# Revit family: PRD_AR_PprTwlDspnsrs_RODANElectronicPaperTowelDispenser_RODX630
name_source: partatom
category: Specialty Equipment
revit_build: Autodesk Revit 2018 (Build: 20190510_1515(x64)
units: mm (PartAtom-declared; Revit-internal decimal feet)

## family parameters
Cut with Voids When Loaded = Yes
Host = Face
OmniClass Number = 23.40.20.21.17
OmniClass Title = Paper Towel Dispensers, Disposal Units
Part Type = Normal
Room Calculation Point = No
Round Connector Dimension = Use Diameter
Shared = No

## types (1)
- RODX630
    AssetType = Fixed
    BIMObjectName = PRD_AR_PaperTowelDispensers_RODANElectronicPaperTowelDispenser_RODX630
    Category = Pr_40_70_22_62, Paper Towel Dispensers
    Default Elevation = 850 mm  [stored 2.78871 ft]
    Description = Touch free paper towel dispenser for wall mounting, stainless steel, surface satin finished, material thickness 0.8 mm, folded cover with cylinder lock and standard KWC key, infrared sensor activity for non-touch operation, integrated tear-off edge, needs 4 pcs. standard D 1.5 V batteries, maintenance free mechanic and easy paper roll change mechanism, for rolls with max. width 205 mm and max. diameter 200 mm, paper length adjustable to 200, 250 and 300 mm, includes stainless steel screws and dowels.
    DispenserMaterial = PRD_AR_StainlessSteel_SatinFinished
    DurationUnit = year
    Features = stainless steel, surface satin finished
    FillingQuantity = 1
    FillingQuantityUom = Rolls
    Finish = satin finished
    GrossWeight = 6.34 kg
    IfcExportAs = IfcFurnitureType
    IfcExportType = USERDEFINED
    IntegralAccessories = incl. stainless steel screws and dowels
    IsBuiltIn = TRUE
    Lock = Key-lock
    MainColor = stainless steel
    Manufacturer = KWC Group AG
    ManufacturerName = KWC Group AG
    ManufacturerURL = www.kwc.com
    Material = stainless steel
    MaterialCode = 1.4301
    MaterialThickness = 0.80 mm
    MaximumDepthDiameterOfConsumable = 220.00 mm
    MaximumWidthOfConsumable = 205.00 mm
    Model = RODX630
    ModelNumber = 2000090071
    ModelReference = RODX630
    NBSDescription = Paper towel dispensers
    NBSReference = 45-35-72/344
    Name = Electronic Paper Towel Dispenser RODX630
    NetWeight = 5.55 kg
    NominalDepth = 226 mm  [stored 0.74147 ft]
    NominalHeight = 390 mm  [stored 1.27953 ft]
    NominalWidth = 290 mm  [stored 0.951444 ft]
    NumberOfBatteries = 4
    Offset = 0 mm  [stored 0 ft]
    ProductInformation = https://pim.kwc.com
    Size = 290 x 390 x 226 mm
    Style = Dispenser
    TypeOfBatteries = D Mono battery 1.5 V
    TypeOfConsumable = Paper roll
    TypeOfFixing = Screw
    TypeOfMounting = Wall mounting
    TypeOfOperation = Sensor operation
    URL = www.kwc.com
    Uniclass2015Code = Pr_40_70_22_62
    Uniclass2015Title = Paper towel dispensers
    Uniclass2015Version = Products v1.17
    Version = 1
    WarrantyDurationUnit = year

note: [stored X ft] marks values corroborated as IEEE doubles in the binary element streams (Revit-internal decimal feet)

## geometry (parser evidence)
native form markers: Sweep x5
no freeform markers — native parametric forms only
